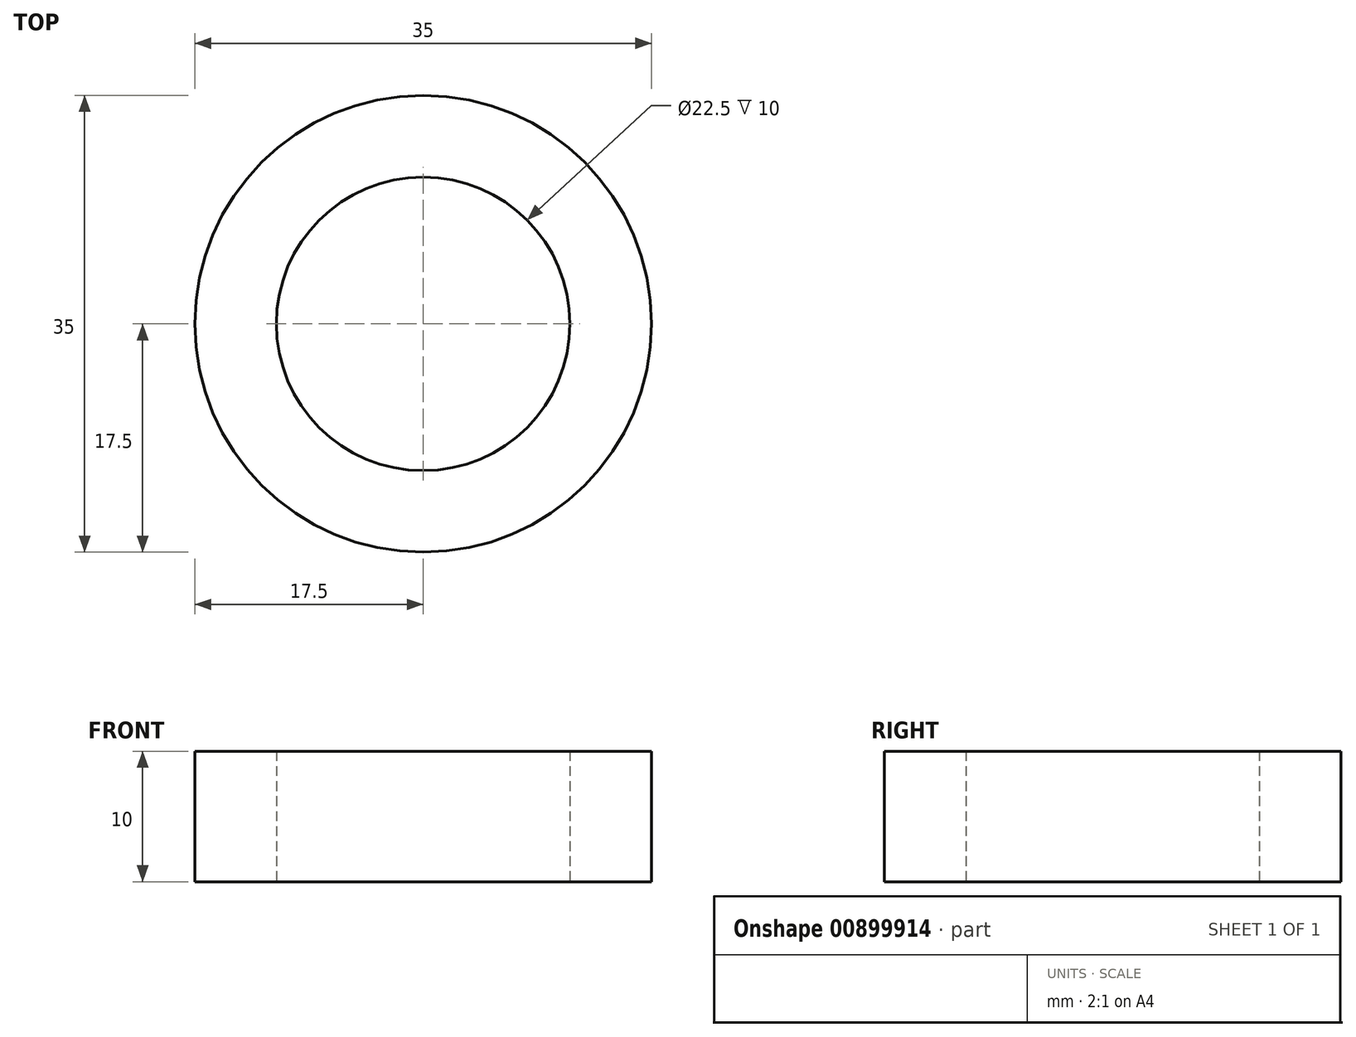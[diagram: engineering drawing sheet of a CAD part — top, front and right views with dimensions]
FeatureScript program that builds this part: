
annotation { "Feature Type Name" : "Feature", "Feature Type Description" : "" }
export const myFeature = defineFeature(function(context is Context, id is Id, definition is map)
    precondition{}
    {
        {
            var Q0;
            Q0=qCreatedBy(makeId("Top.planeOp"),FACE);
            var sketch = newSketch(context, id + "F0", { "sketchPlane" : qUnion([Q0])});
            skCircle(sketch, "E0", {"center": v(0, 0) * mm, "radius": 11.25 * mm});
            skCircle(sketch, "E1", {"center": v(0, 0) * mm, "radius": 17.5 * mm});
            skSolve(sketch);
        }
        {
            var Q0;
            Q0=makeQuery(id+"F0.imprint","IMPRINT",FACE,{"disambiguationData":[TD([[makeQuery(id+"F0.imprint","IMPRINT",EDGE,{"derivedFrom":sQuery(id+"F0.wireOp",EDGE,"E0")}),-1.0]])]});
            extrude(context, id + "F1", {"entities" : qUnion([Q0]), "depth" : 10 * mm, "offsetDistance" : 25 * mm});
        }
    });
